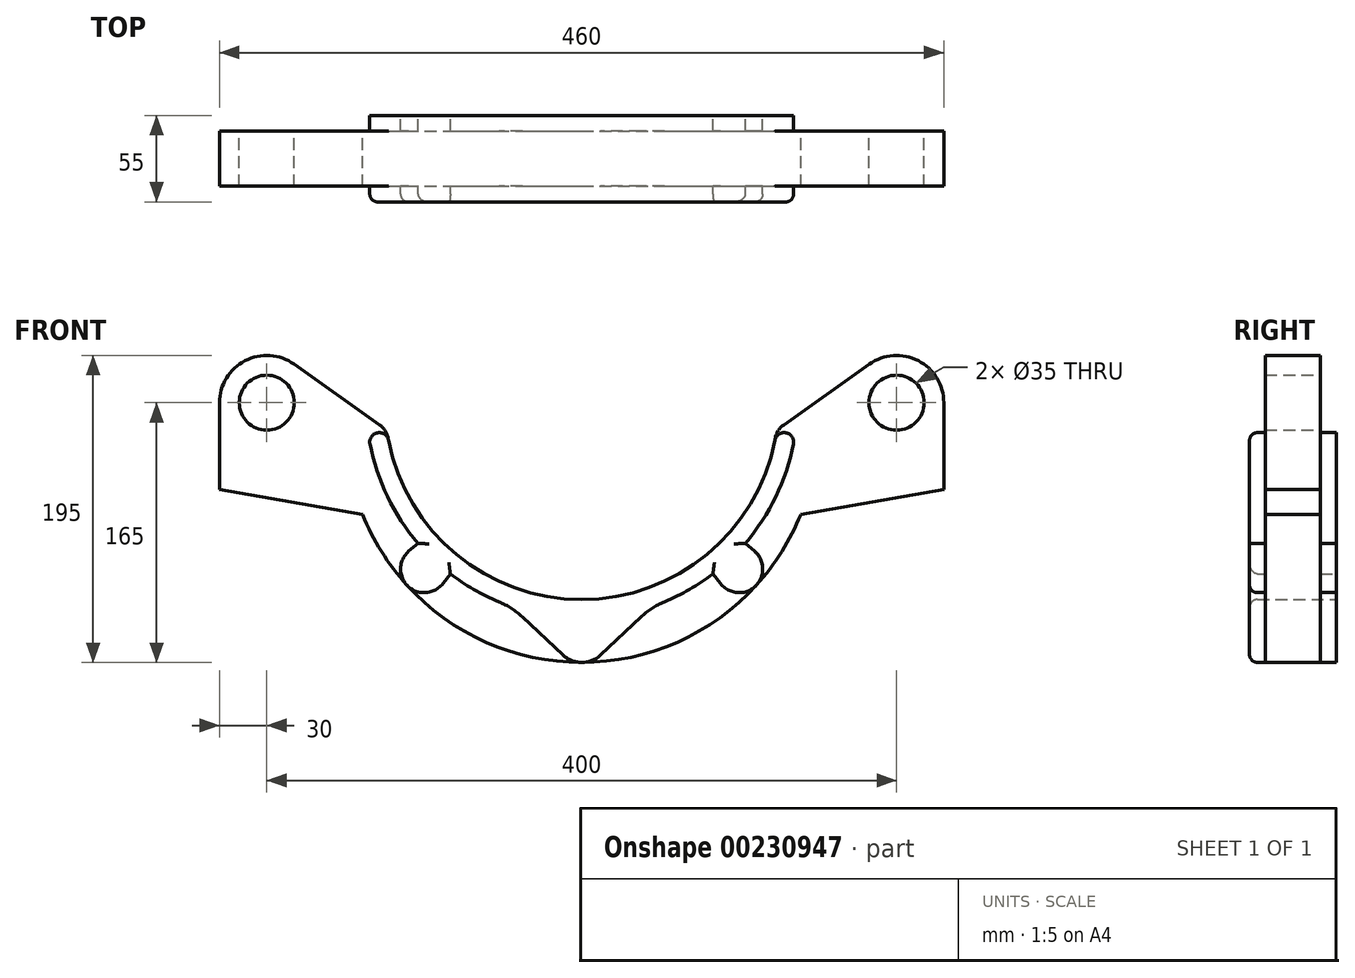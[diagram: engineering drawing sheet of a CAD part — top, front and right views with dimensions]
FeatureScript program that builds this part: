
annotation { "Feature Type Name" : "Feature", "Feature Type Description" : "" }
export const myFeature = defineFeature(function(context is Context, id is Id, definition is map)
    precondition{}
    {
        {
            var Q0;
            Q0=qCreatedBy(makeId("Front.planeOp"),FACE);
            var sketch = newSketch(context, id + "F0", { "sketchPlane" : qUnion([Q0])});
            skArc(sketch, "E0", {"start": v(-122.95, -22.57) * mm, "mid": v(-80.01, -96.04) * mm, "end": v(0, -125) * mm});
            skArc(sketch, "E1", {"start": v(-139.15, -71.02) * mm, "mid": v(-83.96, -139.3) * mm, "end": v(0, -165) * mm});
            skPoint(sketch, "E2.visualSharp", {"position": v(-195, 0) * mm});
            skCircle(sketch, "E3", {"center": v(-200, 0) * mm, "radius": 17.5 * mm});
            skArc(sketch, "E4", {"start": v(-122.95, -22.57) * mm, "mid": v(-124.83, -17.77) * mm, "end": v(-128.4, -14.03) * mm});
            skArc(sketch, "E5", {"start": v(-182.64, 24.47) * mm, "mid": v(-213.77, 26.65) * mm, "end": v(-230, 0) * mm});
            skLineSegment(sketch, "E6", {"start": v(-230, 0) * mm, "end": v(-230, -55) * mm});
            skLineSegment(sketch, "E7", {"start": v(-230, -55) * mm, "end": v(-139.15, -71.02) * mm});
            skLineSegment(sketch, "E8", {"start": v(-128.4, -14.03) * mm, "end": v(-182.64, 24.47) * mm});
            skArc(sketch, "E9.MirrorCS", {"start": v(122.95, -22.57) * mm, "mid": v(124.83, -17.77) * mm, "end": v(128.4, -14.03) * mm});
            skLineSegment(sketch, "E10.MirrorCS", {"start": v(230, -55) * mm, "end": v(139.15, -71.02) * mm});
            skArc(sketch, "E11.MirrorCS", {"start": v(122.95, -22.57) * mm, "mid": v(80.01, -96.04) * mm, "end": v(0, -125) * mm});
            skLineSegment(sketch, "E12.MirrorCS", {"start": v(230, 0) * mm, "end": v(230, -55) * mm});
            skLineSegment(sketch, "E13.MirrorCS", {"start": v(128.4, -14.03) * mm, "end": v(182.64, 24.47) * mm});
            skArc(sketch, "E14.MirrorCS", {"start": v(139.15, -71.02) * mm, "mid": v(83.96, -139.3) * mm, "end": v(0, -165) * mm});
            skPoint(sketch, "E15.MirrorP", {"position": v(195, 0) * mm});
            skArc(sketch, "E16.MirrorCS", {"start": v(182.64, 24.47) * mm, "mid": v(213.77, 26.65) * mm, "end": v(230, 0) * mm});
            skCircle(sketch, "E17.MirrorC", {"center": v(200, 0) * mm, "radius": 17.5 * mm});
            skSolve(sketch);
        }
        {
            var Q0;
            Q0 = qSketchRegion(id + "F0", true);
            extrude(context, id + "F1", {"entities" : qUnion([Q0]), "depth" : 35 * mm, "symmetric" : true});
        }
        {
            var Q0;
            Q0=qCreatedBy(makeId("Front.planeOp"),FACE);
            var sketch = newSketch(context, id + "F2", { "sketchPlane" : qUnion([Q0])});
            skArc(sketch, "E18", {"start": v(-134.48, -26.15) * mm, "mid": v(-123.3, -59.7) * mm, "end": v(-103.91, -89.28) * mm});
            skArc(sketch, "E19", {"start": v(-122.7, -23.85) * mm, "mid": v(0, -125) * mm, "end": v(122.7, -23.85) * mm});
            skArc(sketch, "E20", {"start": v(-122.7, -23.85) * mm, "mid": v(-129.74, -19.11) * mm, "end": v(-134.48, -26.15) * mm});
            skArc(sketch, "E21", {"start": v(134.48, -26.15) * mm, "mid": v(129.74, -19.11) * mm, "end": v(122.7, -23.85) * mm});
            skArc(sketch, "E22", {"start": v(-11.98, -160.25) * mm, "mid": v(0, -165) * mm, "end": v(11.98, -160.25) * mm});
            skArc(sketch, "E23.trimOffspring", {"start": v(52.6, -126.5) * mm, "mid": v(68.58, -118.6) * mm, "end": v(83.4, -108.7) * mm});
            skArc(sketch, "E24", {"start": v(-109.78, -94.31) * mm, "mid": v(-110.3, -116.59) * mm, "end": v(-88.1, -114.82) * mm});
            skArc(sketch, "E25", {"start": v(88.1, -114.82) * mm, "mid": v(110.3, -116.59) * mm, "end": v(109.78, -94.31) * mm});
            skLineSegment(sketch, "E26", {"start": v(-103.91, -89.28) * mm, "end": v(-109.78, -94.31) * mm});
            skLineSegment(sketch, "E27", {"start": v(-83.4, -108.7) * mm, "end": v(-88.1, -114.82) * mm});
            skLineSegment(sketch, "E28", {"start": v(83.4, -108.7) * mm, "end": v(88.1, -114.82) * mm});
            skLineSegment(sketch, "E29", {"start": v(103.91, -89.28) * mm, "end": v(109.78, -94.31) * mm});
            skArc(sketch, "E30.trimOffspring", {"start": v(-83.4, -108.7) * mm, "mid": v(-68.58, -118.6) * mm, "end": v(-52.6, -126.5) * mm});
            skArc(sketch, "E31.trimOffspring", {"start": v(103.91, -89.28) * mm, "mid": v(123.3, -59.7) * mm, "end": v(134.48, -26.15) * mm});
            skLineSegment(sketch, "E32", {"start": v(-11.98, -160.25) * mm, "end": v(-37.55, -136.23) * mm});
            skLineSegment(sketch, "E33", {"start": v(11.98, -160.25) * mm, "end": v(37.55, -136.23) * mm});
            skPoint(sketch, "E34.visualSharp", {"position": v(-44.72, -129.5) * mm});
            skArc(sketch, "E34.filletArc", {"start": v(-37.55, -136.23) * mm, "mid": v(-44.63, -130.69) * mm, "end": v(-52.6, -126.5) * mm});
            skPoint(sketch, "E35.visualSharp", {"position": v(44.72, -129.5) * mm});
            skArc(sketch, "E35.filletArc", {"start": v(52.6, -126.5) * mm, "mid": v(44.63, -130.69) * mm, "end": v(37.55, -136.23) * mm});
            skSolve(sketch);
        }
        {
            var Q0;
            Q0 = qSketchRegion(id + "F2", true);
            extrude(context, id + "F3", {"entities" : qUnion([Q0]), "operationType" : NewBodyOperationType.ADD, "depth" : 55 * mm, "symmetric" : true});
        }
        {
            var Q0;
            Q0=makeQuery(id+"F3.opExtrude","CAP_FACE",FACE,{"disambiguationData":[OSD([sQuery(id+"F2.wireOp",EDGE,"E18"),sQuery(id+"F2.wireOp",EDGE,"E19"),sQuery(id+"F2.wireOp",EDGE,"E20"),sQuery(id+"F2.wireOp",EDGE,"E21"),sQuery(id+"F2.wireOp",EDGE,"E22"),sQuery(id+"F2.wireOp",EDGE,"E23.trimOffspring"),sQuery(id+"F2.wireOp",EDGE,"E24"),sQuery(id+"F2.wireOp",EDGE,"E25"),sQuery(id+"F2.wireOp",EDGE,"E26"),sQuery(id+"F2.wireOp",EDGE,"E27"),sQuery(id+"F2.wireOp",EDGE,"E28"),sQuery(id+"F2.wireOp",EDGE,"E29"),sQuery(id+"F2.wireOp",EDGE,"E30.trimOffspring"),sQuery(id+"F2.wireOp",EDGE,"E31.trimOffspring"),sQuery(id+"F2.wireOp",EDGE,"E32"),sQuery(id+"F2.wireOp",EDGE,"E33"),sQuery(id+"F2.wireOp",EDGE,"E34.filletArc"),sQuery(id+"F2.wireOp",EDGE,"E35.filletArc")])],"isStart":false});
            fillet(context, id + "F4", {"entities" : qUnion([Q0]), "radius" : 5 * mm, "tangentPropagation" : true, "defaultsChanged" : true, "allowEdgeOverflow" : false, "vertexSettings" : [], "filletType" : FilletType.EDGE});
        }
    });
